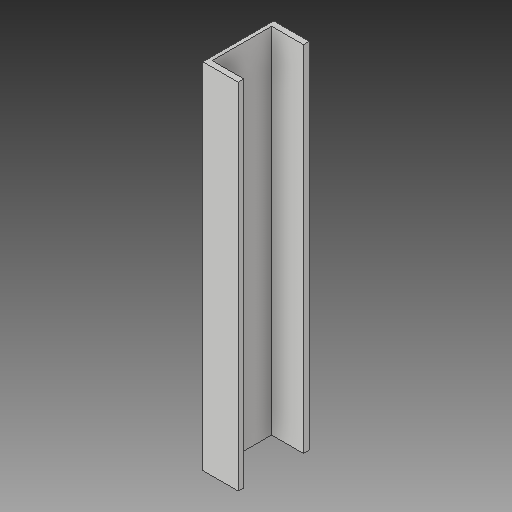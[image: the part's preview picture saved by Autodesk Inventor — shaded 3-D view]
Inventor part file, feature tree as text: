
AUTODESK INVENTOR PART (.ipt)
format: ipt  version: 2019 (Build 230136000, 136)  size: 91,136 bytes
history: native  units: in
note: dims shown in document units (in); Inventor stores cm internally (conversion verified against a paired STEP export)
features: other x3, sketch x1
ambient origin geometry x8: Origin, YZ Plane, XZ Plane, XY Plane, X Axis, Y Axis, Z Axis, Center Point
bodies: Solid1 (feature_tree)
feature tree (4):
  other  "Channel1.ipt"
  other  "Solid1::Channel1.ipt"
  other  "TaggingFeature1"
  sketch  "Sketch1"  dims[d0=0.3937in]
